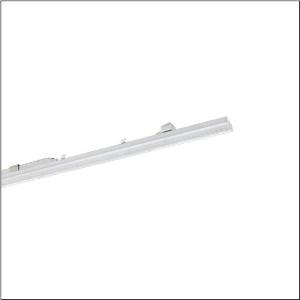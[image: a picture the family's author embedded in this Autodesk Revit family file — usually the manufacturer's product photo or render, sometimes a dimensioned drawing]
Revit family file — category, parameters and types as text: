
# Revit family: tl_l_5wd7a8f0a2b5
name_source: partatom
category: Lighting Fixtures
units: mm (PartAtom-declared; Revit-internal decimal feet)

## family parameters
Cut with Voids When Loaded = No
Host = Face
Light Source = No
Part Type = Normal
Room Calculation Point = No
Round Connector Dimension = Use Diameter
Shared = No

## types (1)
- TL L (1 x LED, 4990 lm, 30 W, 4000K)
    Apparent Load = 30 VA
    CIE Flux Codes = 49 84 98 100 100
    Color Rendering = 80
    Color Temperature = 4000K
    Default Elevation = 1800 mm
    Description = TL L, luminaire insert, of sheet steel, galvanised, coil coated, white, length: 1.500mm, width: 66mm, height: 67mm, LED rated luminous flux: 4.990lm, light colour: 840, control gear: 4..20mA, with terminal, 5-pole, mains connection: 230..240V, AC, 50/60Hz, rated input power: 30W, primary optical cover: cover, of PMMA, light emission: direct distribution, protection rating (complete): as luminaire, insulation class (complete): insulation class I (protective earthing), certification: CE, impact resistance: IK06, permissible ambient temperature for indoor applications: -25..+35°C, packaging unit: 1 piece
    Height = 120 mm
    Lamp = 1 x LED
    Lamp Light Flux = 4990 lm
    Lamp Power = 30 W
    Lamp count = 1
    Length = 1690 mm
    Luminous efficacy = 166 lm/W
    Manufacturer = Siteco
    ModVariant = No
    Model = 5WD7A8F0A2B5
    Mounting Place = Ceiling
    Mounting Type = Pendant
    Number of Poles = 1
    OnlyDefault = Yes
    Power Factor = 1
    Product Name = TL L
    Product group = luminaire insert
    ProductGroupID = 901
    Protection Class = Protection class I
    Protection Degree = Degree of protection
    RLX_Detail_Level = 1
    RLX_Emergency_Light_Flux = 0 lm
    RLX_Emergency_Type = 0
    RLX_Emergency_Type_DB = No
    RlxData = <blob elided: 14093 chars, md5=4e40bacb>
    Socket = socket
    Standby Power = 0 W
    System Light Flux = 4990 lm
    System Power = 30 W
    Type Comments = Product without accessories
    Type Image = l_1294382.jpg
    URL = http://relux.com
    VarID = ---
    Voltage = 0 V
    Weight = 0.00 kg
    Width = 208 mm

## geometry (parser evidence)
native form markers: Sweep x13
no freeform markers — native parametric forms only
